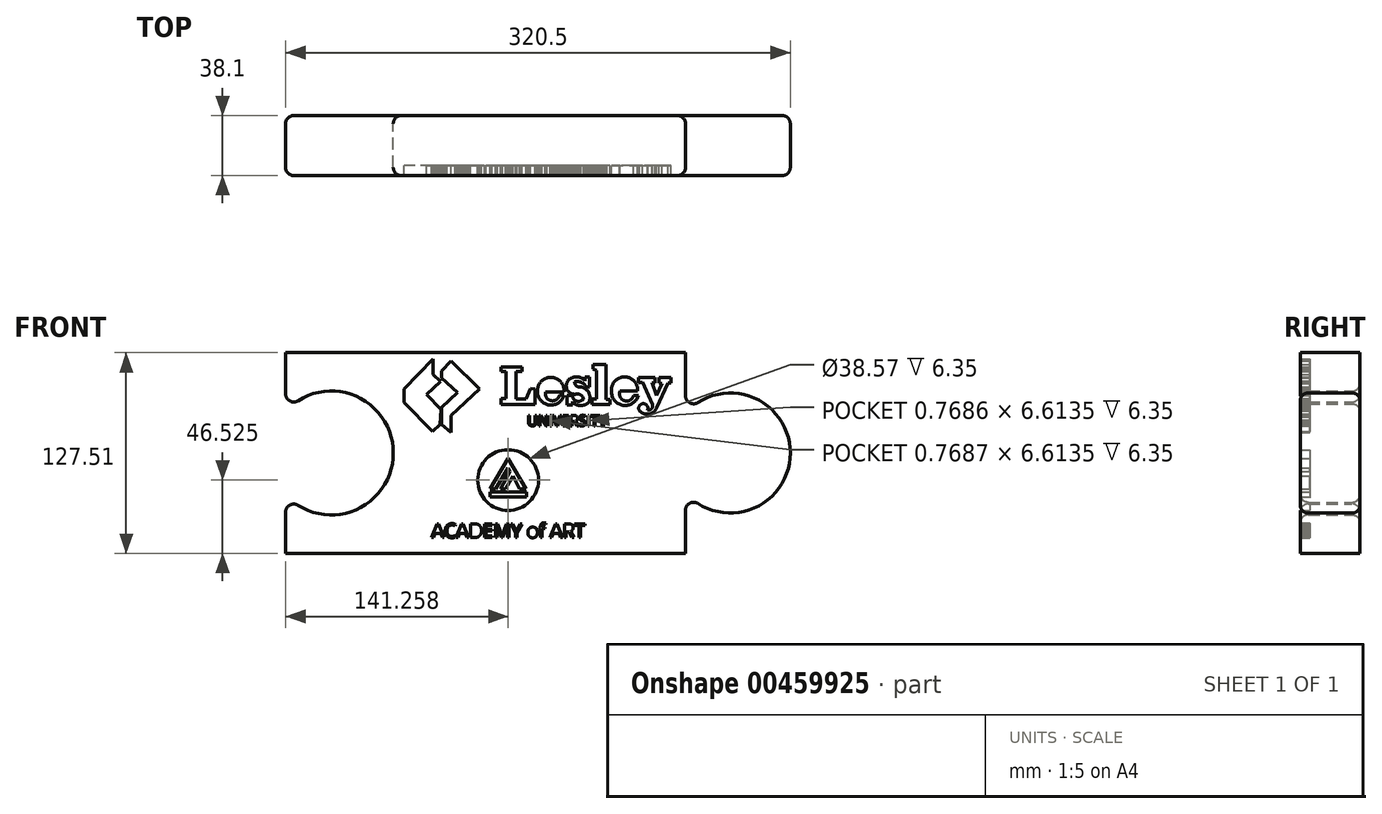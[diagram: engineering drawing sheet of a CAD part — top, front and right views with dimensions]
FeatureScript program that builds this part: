
annotation { "Feature Type Name" : "Feature", "Feature Type Description" : "" }
export const myFeature = defineFeature(function(context is Context, id is Id, definition is map)
    precondition{}
    {
        {
            var Q0;
            Q0=qCreatedBy(makeId("Front.planeOp"),FACE);
            var sketch = newSketch(context, id + "F0", { "sketchPlane" : qUnion([Q0])});
            skLineSegment(sketch, "E0", {"start": v(-231.22, 105.6) * mm, "end": v(22.78, 105.6) * mm});
            skLineSegment(sketch, "E1", {"start": v(-231.22, -21.9) * mm, "end": v(22.78, -21.9) * mm});
            skArc(sketch, "E2", {"start": v(22.78, 16.45) * mm, "mid": v(89.28, 41.85) * mm, "end": v(22.78, 67.25) * mm});
            skLineSegment(sketch, "E3", {"start": v(22.78, 67.25) * mm, "end": v(22.78, 105.6) * mm});
            skLineSegment(sketch, "E4", {"start": v(22.78, 16.45) * mm, "end": v(22.78, -21.9) * mm});
            skArc(sketch, "E5", {"start": v(-231.22, 15.18) * mm, "mid": v(-162.9, 41.85) * mm, "end": v(-231.22, 68.52) * mm});
            skLineSegment(sketch, "E6", {"start": v(-231.22, 15.18) * mm, "end": v(-231.22, -21.9) * mm});
            skLineSegment(sketch, "E7", {"start": v(-231.22, 68.52) * mm, "end": v(-231.22, 105.6) * mm});
            skCircle(sketch, "E8", {"center": v(-89.96, 24.62) * mm, "radius": 19.29 * mm});
            skText(sketch, "E9", { "text": "ACADEMY of ART", "fontName": "OpenSans-Regular.ttf"});
            skLineSegment(sketch, "E10", {"start": v(-132.08, 89.6) * mm, "end": v(-122.02, 80.37) * mm});
            skLineSegment(sketch, "E11", {"start": v(-132.08, 89.6) * mm, "end": v(-132.08, 94.1) * mm});
            skLineSegment(sketch, "E12", {"start": v(-132.08, 94.1) * mm, "end": v(-119.6, 82.65) * mm});
            skLineSegment(sketch, "E13", {"start": v(-119.6, 82.65) * mm, "end": v(-132.08, 70.9) * mm});
            skLineSegment(sketch, "E14", {"start": v(-132.08, 70.9) * mm, "end": v(-126.27, 65.56) * mm});
            skLineSegment(sketch, "E15", {"start": v(-126.27, 65.56) * mm, "end": v(-126.27, 54.88) * mm});
            skLineSegment(sketch, "E16", {"start": v(-126.27, 54.88) * mm, "end": v(-107.94, 73.88) * mm});
            skLineSegment(sketch, "E17", {"start": v(-108.11, 73.7) * mm, "end": v(-108.11, 82.65) * mm});
            skLineSegment(sketch, "E18", {"start": v(-108.11, 82.65) * mm, "end": v(-126.27, 65.56) * mm});
            skLineSegment(sketch, "E19", {"start": v(-132.08, 94.1) * mm, "end": v(-126.27, 100.43) * mm});
            skLineSegment(sketch, "E20", {"start": v(-126.27, 100.43) * mm, "end": v(-108.11, 82.65) * mm});
            skLineSegment(sketch, "E21", {"start": v(-137.7, 101.62) * mm, "end": v(-137.7, 91.84) * mm});
            skPoint(sketch, "E21.endSnap0", {"position": v(-132.08, 91.84) * mm});
            skLineSegment(sketch, "E22", {"start": v(-137.7, 91.84) * mm, "end": v(-156.08, 73.88) * mm});
            skPoint(sketch, "E22.endSnap0", {"position": v(-156.08, 78.25) * mm});
            skLineSegment(sketch, "E23", {"start": v(-156.08, 82.65) * mm, "end": v(-156.08, 73.88) * mm});
            skLineSegment(sketch, "E24", {"start": v(-156.08, 82.65) * mm, "end": v(-137.7, 101.62) * mm});
            skLineSegment(sketch, "E25", {"start": v(-156.08, 73.88) * mm, "end": v(-138, 55.4) * mm});
            skLineSegment(sketch, "E26", {"start": v(-138, 55.4) * mm, "end": v(-133.18, 60.1) * mm});
            skLineSegment(sketch, "E27", {"start": v(-132.08, 70.9) * mm, "end": v(-132.08, 60.1) * mm});
            skLineSegment(sketch, "E28", {"start": v(-132.08, 60.1) * mm, "end": v(-126.27, 54.88) * mm});
            skLineSegment(sketch, "E29", {"start": v(-146.49, 73.88) * mm, "end": v(-133.18, 60.1) * mm});
            skLineSegment(sketch, "E30", {"start": v(-94.5, 93.55) * mm, "end": v(-94.5, 96.58) * mm});
            skLineSegment(sketch, "E31", {"start": v(-94.5, 96.58) * mm, "end": v(-81.08, 96.58) * mm});
            skLineSegment(sketch, "E32", {"start": v(-81.08, 96.58) * mm, "end": v(-81.08, 93.77) * mm});
            skLineSegment(sketch, "E33", {"start": v(-81.08, 93.77) * mm, "end": v(-85.05, 93.77) * mm});
            skLineSegment(sketch, "E34", {"start": v(-85.05, 93.77) * mm, "end": v(-85.05, 76.1) * mm});
            skLineSegment(sketch, "E35", {"start": v(-85.05, 76.1) * mm, "end": v(-78.52, 76.1) * mm});
            skLineSegment(sketch, "E36", {"start": v(-78.52, 76.1) * mm, "end": v(-75.83, 82.81) * mm});
            skLineSegment(sketch, "E37", {"start": v(-94.5, 93.55) * mm, "end": v(-91.3, 93.55) * mm});
            skLineSegment(sketch, "E38", {"start": v(-91.3, 93.55) * mm, "end": v(-91.3, 76.56) * mm});
            skLineSegment(sketch, "E39", {"start": v(-91.3, 76.56) * mm, "end": v(-94.5, 76.56) * mm});
            skLineSegment(sketch, "E40", {"start": v(-94.5, 76.56) * mm, "end": v(-94.5, 72.76) * mm});
            skLineSegment(sketch, "E41", {"start": v(-94.5, 72.76) * mm, "end": v(-72.7, 72.76) * mm});
            skLineSegment(sketch, "E42", {"start": v(-72.7, 72.76) * mm, "end": v(-72.7, 82.57) * mm});
            skLineSegment(sketch, "E43", {"start": v(-72.7, 82.57) * mm, "end": v(-75.83, 82.81) * mm});
            skLineSegment(sketch, "E44", {"start": v(-57.35, 78.56) * mm, "end": v(-54.4, 78.56) * mm});
            skLineSegment(sketch, "E45", {"start": v(-65.7, 82.57) * mm, "end": v(-59.8, 82.57) * mm});
            skLineSegment(sketch, "E46", {"start": v(-66.16, 80.54) * mm, "end": v(-54.4, 80.54) * mm});
            skArc(sketch, "E47", {"start": v(-59.8, 82.57) * mm, "mid": v(-62.76, 87.36) * mm, "end": v(-65.7, 82.57) * mm});
            skArc(sketch, "E48", {"start": v(-54.4, 80.54) * mm, "mid": v(-62.85, 89.89) * mm, "end": v(-71.3, 80.54) * mm});
            skArc(sketch, "E49", {"start": v(-71.3, 80.54) * mm, "mid": v(-63.7, 72.33) * mm, "end": v(-54.4, 78.56) * mm});
            skArc(sketch, "E50", {"start": v(-66.16, 80.54) * mm, "mid": v(-62.75, 75.11) * mm, "end": v(-57.35, 78.56) * mm});
            skLineSegment(sketch, "E51", {"start": v(-18.82, 81.15) * mm, "end": v(-7.64, 81.15) * mm});
            skLineSegment(sketch, "E52", {"start": v(-19.2, 83.23) * mm, "end": v(-12.95, 83.23) * mm});
            skLineSegment(sketch, "E53", {"start": v(-10.3, 78.5) * mm, "end": v(-7.26, 78.5) * mm});
            skLineSegment(sketch, "E54", {"start": v(-40.4, 83.88) * mm, "end": v(-38.13, 83.88) * mm});
            skLineSegment(sketch, "E55", {"start": v(-38.13, 83.88) * mm, "end": v(-38.13, 90.14) * mm});
            skLineSegment(sketch, "E56", {"start": v(-38.13, 90.14) * mm, "end": v(-40.97, 90.14) * mm});
            skLineSegment(sketch, "E57", {"start": v(-40.97, 90.14) * mm, "end": v(-40.97, 87.68) * mm});
            skLineSegment(sketch, "E58", {"start": v(-49.16, 74.51) * mm, "end": v(-49.16, 72.24) * mm});
            skLineSegment(sketch, "E59", {"start": v(-49.16, 72.24) * mm, "end": v(-52.58, 72.24) * mm});
            skLineSegment(sketch, "E60", {"start": v(-52.58, 72.24) * mm, "end": v(-52.58, 78.5) * mm});
            skLineSegment(sketch, "E61", {"start": v(-52.58, 78.5) * mm, "end": v(-49.16, 78.5) * mm});
            skLineSegment(sketch, "E62", {"start": v(-36.08, 95.18) * mm, "end": v(-36.08, 98.21) * mm});
            skLineSegment(sketch, "E63", {"start": v(-36.08, 98.21) * mm, "end": v(-27.93, 98.21) * mm});
            skLineSegment(sketch, "E64", {"start": v(-27.93, 98.21) * mm, "end": v(-27.93, 75.84) * mm});
            skLineSegment(sketch, "E65", {"start": v(-27.93, 75.84) * mm, "end": v(-25.08, 75.84) * mm});
            skLineSegment(sketch, "E66", {"start": v(-25.08, 75.84) * mm, "end": v(-25.08, 72.8) * mm});
            skLineSegment(sketch, "E67", {"start": v(-25.08, 72.8) * mm, "end": v(-36.65, 72.8) * mm});
            skLineSegment(sketch, "E68", {"start": v(-36.65, 72.8) * mm, "end": v(-36.65, 76.03) * mm});
            skLineSegment(sketch, "E69", {"start": v(-36.65, 76.03) * mm, "end": v(-33.8, 76.03) * mm});
            skLineSegment(sketch, "E70", {"start": v(-33.8, 76.03) * mm, "end": v(-33.8, 94.23) * mm});
            skLineSegment(sketch, "E71", {"start": v(-33.8, 94.23) * mm, "end": v(-36.08, 95.18) * mm});
            skLineSegment(sketch, "E72", {"start": v(1.53, 86.65) * mm, "end": v(4.3, 78.3) * mm});
            skLineSegment(sketch, "E73", {"start": v(4.3, 78.3) * mm, "end": v(7.91, 86.08) * mm});
            skLineSegment(sketch, "E74", {"start": v(6.02, 86.27) * mm, "end": v(7.91, 86.08) * mm});
            skLineSegment(sketch, "E75", {"start": v(6.02, 86.27) * mm, "end": v(6.02, 89.68) * mm});
            skLineSegment(sketch, "E76", {"start": v(6.02, 89.68) * mm, "end": v(13.43, 89.68) * mm});
            skLineSegment(sketch, "E77", {"start": v(13.43, 89.68) * mm, "end": v(13.43, 86.27) * mm});
            skLineSegment(sketch, "E78", {"start": v(13.43, 86.27) * mm, "end": v(11.7, 86.27) * mm});
            skLineSegment(sketch, "E79", {"start": v(11.7, 86.27) * mm, "end": v(4.3, 70.34) * mm});
            skLineSegment(sketch, "E80", {"start": v(1.62, 72.78) * mm, "end": v(-4.6, 86.84) * mm});
            skLineSegment(sketch, "E81", {"start": v(1.53, 86.65) * mm, "end": v(3.36, 86.27) * mm});
            skLineSegment(sketch, "E82", {"start": v(3.36, 86.27) * mm, "end": v(3.36, 89.68) * mm});
            skLineSegment(sketch, "E83", {"start": v(3.36, 89.68) * mm, "end": v(-7.26, 89.68) * mm});
            skLineSegment(sketch, "E84", {"start": v(-7.26, 89.68) * mm, "end": v(-7.26, 86.27) * mm});
            skLineSegment(sketch, "E85", {"start": v(-7.26, 86.27) * mm, "end": v(-4.6, 86.84) * mm});
            skArc(sketch, "E86", {"start": v(-1.38, 69.2) * mm, "mid": v(1.24, 70.06) * mm, "end": v(1.62, 72.78) * mm});
            skArc(sketch, "E87", {"start": v(-6.5, 68.63) * mm, "mid": v(-0.64, 66.6) * mm, "end": v(4.3, 70.34) * mm});
            skArc(sketch, "E88", {"start": v(-7.64, 81.15) * mm, "mid": v(-15.98, 90.2) * mm, "end": v(-24.32, 81.15) * mm});
            skArc(sketch, "E89", {"start": v(-24.32, 81.15) * mm, "mid": v(-16.98, 72.19) * mm, "end": v(-7.26, 78.5) * mm});
            skArc(sketch, "E90", {"start": v(-18.82, 81.15) * mm, "mid": v(-16.04, 75.07) * mm, "end": v(-10.3, 78.5) * mm});
            skArc(sketch, "E91", {"start": v(-12.95, 83.23) * mm, "mid": v(-16.07, 87.66) * mm, "end": v(-19.2, 83.23) * mm});
            skArc(sketch, "E92", {"start": v(-49.16, 78.5) * mm, "mid": v(-46.47, 74.84) * mm, "end": v(-42.15, 76.22) * mm});
            skArc(sketch, "E93", {"start": v(-42.15, 76.22) * mm, "mid": v(-43.8, 78.75) * mm, "end": v(-46.77, 79.23) * mm});
            skArc(sketch, "E94", {"start": v(-49.27, 89.73) * mm, "mid": v(-52.9, 83.32) * mm, "end": v(-46.77, 79.23) * mm});
            skArc(sketch, "E95", {"start": v(-40.97, 87.68) * mm, "mid": v(-44.79, 90.07) * mm, "end": v(-49.27, 89.73) * mm});
            skArc(sketch, "E96", {"start": v(-40.4, 83.88) * mm, "mid": v(-43.46, 86.77) * mm, "end": v(-47.65, 87) * mm});
            skArc(sketch, "E97", {"start": v(-47.65, 87) * mm, "mid": v(-46.56, 84.41) * mm, "end": v(-43.8, 83.88) * mm});
            skArc(sketch, "E98", {"start": v(-49.16, 74.51) * mm, "mid": v(-43.8, 71.98) * mm, "end": v(-38.45, 74.51) * mm});
            skArc(sketch, "E99", {"start": v(-38.45, 74.51) * mm, "mid": v(-38.9, 80.47) * mm, "end": v(-43.8, 83.88) * mm});
            skText(sketch, "E100", { "text": "UNIVERSITY\n", "fontName": "OpenSans-Regular.ttf"});
            skLineSegment(sketch, "E101", {"start": v(-137.7, 101.62) * mm, "end": v(-132.98, 97.04) * mm});
            skLineSegment(sketch, "E102", {"start": v(-132.96, 97.08) * mm, "end": v(-132.96, 87.22) * mm});
            skLineSegment(sketch, "E103", {"start": v(-132.87, 87.4) * mm, "end": v(-141.86, 78.93) * mm});
            skLineSegment(sketch, "E104", {"start": v(-146.49, 73.88) * mm, "end": v(-141.86, 78.93) * mm});
            skLineSegment(sketch, "E105", {"start": v(-137.7, 91.84) * mm, "end": v(-132.87, 87.4) * mm});
            skLineSegment(sketch, "E106", {"start": v(-133.18, 60.1) * mm, "end": v(-132.63, 69.43) * mm});
            skLineSegment(sketch, "E107", {"start": v(-141.86, 78.93) * mm, "end": v(-132.63, 69.43) * mm});
            skArc(sketch, "E108", {"start": v(-1.38, 69.2) * mm, "mid": v(-4.41, 73.2) * mm, "end": v(-6.5, 68.63) * mm});
            const initialGuessF0  = {"E9": [-0.13842, -0.01189, 1, 0, 0.00886], "E100": [-0.07792, 0.05915, 1, 0, 0.00667]};
            skSetInitialGuess(sketch, initialGuessF0);
            skSolve(sketch);
        }
        {
            var Q0;
            Q0 = qSketchRegion(id + "F0", true);
            extrude(context, id + "F1", {"entities" : qUnion([Q0]), "depth" : 38.1 * mm});
        }
        {
            var Q0;
            Q0=makeQuery(id+"F1.opExtrude","CAP_FACE",FACE,{"disambiguationData":[OSD([sQuery(id+"F0.wireOp",EDGE,"E0"),sQuery(id+"F0.wireOp",EDGE,"E1"),sQuery(id+"F0.wireOp",EDGE,"E2"),sQuery(id+"F0.wireOp",EDGE,"E3"),sQuery(id+"F0.wireOp",EDGE,"E4"),sQuery(id+"F0.wireOp",EDGE,"E5"),sQuery(id+"F0.wireOp",EDGE,"E6"),sQuery(id+"F0.wireOp",EDGE,"E7"),sQuery(id+"F0.wireOp",EDGE,"E8"),sQuery(id+"F0.wireOp",EDGE,"E9.sketch_text.stroke-0"),sQuery(id+"F0.wireOp",EDGE,"E9.sketch_text.stroke-1"),sQuery(id+"F0.wireOp",EDGE,"E9.sketch_text.stroke-2"),sQuery(id+"F0.wireOp",EDGE,"E9.sketch_text.stroke-3"),sQuery(id+"F0.wireOp",EDGE,"E9.sketch_text.stroke-4"),sQuery(id+"F0.wireOp",EDGE,"E9.sketch_text.stroke-5"),sQuery(id+"F0.wireOp",EDGE,"E9.sketch_text.stroke-6"),sQuery(id+"F0.wireOp",EDGE,"E9.sketch_text.stroke-7"),sQuery(id+"F0.wireOp",EDGE,"E9.sketch_text.stroke-13"),sQuery(id+"F0.wireOp",EDGE,"E9.sketch_text.stroke-14"),sQuery(id+"F0.wireOp",EDGE,"E9.sketch_text.stroke-15"),sQuery(id+"F0.wireOp",EDGE,"E9.sketch_text.stroke-16"),sQuery(id+"F0.wireOp",EDGE,"E9.sketch_text.stroke-17"),sQuery(id+"F0.wireOp",EDGE,"E9.sketch_text.stroke-18"),sQuery(id+"F0.wireOp",EDGE,"E9.sketch_text.stroke-19"),sQuery(id+"F0.wireOp",EDGE,"E9.sketch_text.stroke-20"),sQuery(id+"F0.wireOp",EDGE,"E9.sketch_text.stroke-21"),sQuery(id+"F0.wireOp",EDGE,"E9.sketch_text.stroke-22"),sQuery(id+"F0.wireOp",EDGE,"E9.sketch_text.stroke-23"),sQuery(id+"F0.wireOp",EDGE,"E9.sketch_text.stroke-24"),sQuery(id+"F0.wireOp",EDGE,"E9.sketch_text.stroke-25"),sQuery(id+"F0.wireOp",EDGE,"E9.sketch_text.stroke-26"),sQuery(id+"F0.wireOp",EDGE,"E9.sketch_text.stroke-27"),sQuery(id+"F0.wireOp",EDGE,"E9.sketch_text.stroke-28"),sQuery(id+"F0.wireOp",EDGE,"E9.sketch_text.stroke-29"),sQuery(id+"F0.wireOp",EDGE,"E9.sketch_text.stroke-30"),sQuery(id+"F0.wireOp",EDGE,"E9.sketch_text.stroke-31"),sQuery(id+"F0.wireOp",EDGE,"E9.sketch_text.stroke-32"),sQuery(id+"F0.wireOp",EDGE,"E9.sketch_text.stroke-33"),sQuery(id+"F0.wireOp",EDGE,"E9.sketch_text.stroke-34"),sQuery(id+"F0.wireOp",EDGE,"E9.sketch_text.stroke-35"),sQuery(id+"F0.wireOp",EDGE,"E9.sketch_text.stroke-41"),sQuery(id+"F0.wireOp",EDGE,"E9.sketch_text.stroke-42"),sQuery(id+"F0.wireOp",EDGE,"E9.sketch_text.stroke-43"),sQuery(id+"F0.wireOp",EDGE,"E9.sketch_text.stroke-44"),sQuery(id+"F0.wireOp",EDGE,"E9.sketch_text.stroke-45"),sQuery(id+"F0.wireOp",EDGE,"E9.sketch_text.stroke-46"),sQuery(id+"F0.wireOp",EDGE,"E9.sketch_text.stroke-47"),sQuery(id+"F0.wireOp",EDGE,"E9.sketch_text.stroke-55"),sQuery(id+"F0.wireOp",EDGE,"E9.sketch_text.stroke-56"),sQuery(id+"F0.wireOp",EDGE,"E9.sketch_text.stroke-57"),sQuery(id+"F0.wireOp",EDGE,"E9.sketch_text.stroke-58"),sQuery(id+"F0.wireOp",EDGE,"E9.sketch_text.stroke-59"),sQuery(id+"F0.wireOp",EDGE,"E9.sketch_text.stroke-60"),sQuery(id+"F0.wireOp",EDGE,"E9.sketch_text.stroke-61"),sQuery(id+"F0.wireOp",EDGE,"E9.sketch_text.stroke-62"),sQuery(id+"F0.wireOp",EDGE,"E9.sketch_text.stroke-63"),sQuery(id+"F0.wireOp",EDGE,"E9.sketch_text.stroke-64"),sQuery(id+"F0.wireOp",EDGE,"E9.sketch_text.stroke-65"),sQuery(id+"F0.wireOp",EDGE,"E9.sketch_text.stroke-66"),sQuery(id+"F0.wireOp",EDGE,"E9.sketch_text.stroke-67"),sQuery(id+"F0.wireOp",EDGE,"E9.sketch_text.stroke-68"),sQuery(id+"F0.wireOp",EDGE,"E9.sketch_text.stroke-69"),sQuery(id+"F0.wireOp",EDGE,"E9.sketch_text.stroke-70"),sQuery(id+"F0.wireOp",EDGE,"E9.sketch_text.stroke-71"),sQuery(id+"F0.wireOp",EDGE,"E9.sketch_text.stroke-72"),sQuery(id+"F0.wireOp",EDGE,"E9.sketch_text.stroke-73"),sQuery(id+"F0.wireOp",EDGE,"E9.sketch_text.stroke-74"),sQuery(id+"F0.wireOp",EDGE,"E9.sketch_text.stroke-75"),sQuery(id+"F0.wireOp",EDGE,"E9.sketch_text.stroke-76"),sQuery(id+"F0.wireOp",EDGE,"E9.sketch_text.stroke-77"),sQuery(id+"F0.wireOp",EDGE,"E9.sketch_text.stroke-78"),sQuery(id+"F0.wireOp",EDGE,"E9.sketch_text.stroke-79"),sQuery(id+"F0.wireOp",EDGE,"E9.sketch_text.stroke-80"),sQuery(id+"F0.wireOp",EDGE,"E9.sketch_text.stroke-81"),sQuery(id+"F0.wireOp",EDGE,"E9.sketch_text.stroke-82"),sQuery(id+"F0.wireOp",EDGE,"E9.sketch_text.stroke-83"),sQuery(id+"F0.wireOp",EDGE,"E9.sketch_text.stroke-84"),sQuery(id+"F0.wireOp",EDGE,"E9.sketch_text.stroke-85"),sQuery(id+"F0.wireOp",EDGE,"E9.sketch_text.stroke-86"),sQuery(id+"F0.wireOp",EDGE,"E9.sketch_text.stroke-87"),sQuery(id+"F0.wireOp",EDGE,"E9.sketch_text.stroke-88"),sQuery(id+"F0.wireOp",EDGE,"E9.sketch_text.stroke-89"),sQuery(id+"F0.wireOp",EDGE,"E9.sketch_text.stroke-90"),sQuery(id+"F0.wireOp",EDGE,"E9.sketch_text.stroke-91"),sQuery(id+"F0.wireOp",EDGE,"E9.sketch_text.stroke-92"),sQuery(id+"F0.wireOp",EDGE,"E9.sketch_text.stroke-93"),sQuery(id+"F0.wireOp",EDGE,"E9.sketch_text.stroke-94"),sQuery(id+"F0.wireOp",EDGE,"E9.sketch_text.stroke-95"),sQuery(id+"F0.wireOp",EDGE,"E9.sketch_text.stroke-96"),sQuery(id+"F0.wireOp",EDGE,"E9.sketch_text.stroke-97"),sQuery(id+"F0.wireOp",EDGE,"E9.sketch_text.stroke-98"),sQuery(id+"F0.wireOp",EDGE,"E9.sketch_text.stroke-99"),sQuery(id+"F0.wireOp",EDGE,"E9.sketch_text.stroke-100"),sQuery(id+"F0.wireOp",EDGE,"E9.sketch_text.stroke-101"),sQuery(id+"F0.wireOp",EDGE,"E9.sketch_text.stroke-102"),sQuery(id+"F0.wireOp",EDGE,"E9.sketch_text.stroke-111"),sQuery(id+"F0.wireOp",EDGE,"E9.sketch_text.stroke-112"),sQuery(id+"F0.wireOp",EDGE,"E9.sketch_text.stroke-113"),sQuery(id+"F0.wireOp",EDGE,"E9.sketch_text.stroke-114"),sQuery(id+"F0.wireOp",EDGE,"E9.sketch_text.stroke-115"),sQuery(id+"F0.wireOp",EDGE,"E9.sketch_text.stroke-116"),sQuery(id+"F0.wireOp",EDGE,"E9.sketch_text.stroke-117"),sQuery(id+"F0.wireOp",EDGE,"E9.sketch_text.stroke-118"),sQuery(id+"F0.wireOp",EDGE,"E9.sketch_text.stroke-119"),sQuery(id+"F0.wireOp",EDGE,"E9.sketch_text.stroke-120"),sQuery(id+"F0.wireOp",EDGE,"E9.sketch_text.stroke-121"),sQuery(id+"F0.wireOp",EDGE,"E9.sketch_text.stroke-122"),sQuery(id+"F0.wireOp",EDGE,"E9.sketch_text.stroke-123"),sQuery(id+"F0.wireOp",EDGE,"E9.sketch_text.stroke-124"),sQuery(id+"F0.wireOp",EDGE,"E9.sketch_text.stroke-125"),sQuery(id+"F0.wireOp",EDGE,"E9.sketch_text.stroke-126"),sQuery(id+"F0.wireOp",EDGE,"E9.sketch_text.stroke-127"),sQuery(id+"F0.wireOp",EDGE,"E9.sketch_text.stroke-128"),sQuery(id+"F0.wireOp",EDGE,"E9.sketch_text.stroke-129"),sQuery(id+"F0.wireOp",EDGE,"E9.sketch_text.stroke-130"),sQuery(id+"F0.wireOp",EDGE,"E9.sketch_text.stroke-131"),sQuery(id+"F0.wireOp",EDGE,"E9.sketch_text.stroke-132"),sQuery(id+"F0.wireOp",EDGE,"E9.sketch_text.stroke-133"),sQuery(id+"F0.wireOp",EDGE,"E9.sketch_text.stroke-134"),sQuery(id+"F0.wireOp",EDGE,"E9.sketch_text.stroke-135"),sQuery(id+"F0.wireOp",EDGE,"E9.sketch_text.stroke-141"),sQuery(id+"F0.wireOp",EDGE,"E9.sketch_text.stroke-142"),sQuery(id+"F0.wireOp",EDGE,"E9.sketch_text.stroke-143"),sQuery(id+"F0.wireOp",EDGE,"E9.sketch_text.stroke-144"),sQuery(id+"F0.wireOp",EDGE,"E9.sketch_text.stroke-145"),sQuery(id+"F0.wireOp",EDGE,"E9.sketch_text.stroke-146"),sQuery(id+"F0.wireOp",EDGE,"E9.sketch_text.stroke-147"),sQuery(id+"F0.wireOp",EDGE,"E9.sketch_text.stroke-148"),sQuery(id+"F0.wireOp",EDGE,"E9.sketch_text.stroke-149"),sQuery(id+"F0.wireOp",EDGE,"E9.sketch_text.stroke-150"),sQuery(id+"F0.wireOp",EDGE,"E9.sketch_text.stroke-151"),sQuery(id+"F0.wireOp",EDGE,"E9.sketch_text.stroke-159"),sQuery(id+"F0.wireOp",EDGE,"E9.sketch_text.stroke-160"),sQuery(id+"F0.wireOp",EDGE,"E9.sketch_text.stroke-161"),sQuery(id+"F0.wireOp",EDGE,"E9.sketch_text.stroke-162"),sQuery(id+"F0.wireOp",EDGE,"E9.sketch_text.stroke-163"),sQuery(id+"F0.wireOp",EDGE,"E9.sketch_text.stroke-164"),sQuery(id+"F0.wireOp",EDGE,"E9.sketch_text.stroke-165"),sQuery(id+"F0.wireOp",EDGE,"E9.sketch_text.stroke-166"),sQuery(id+"F0.wireOp",EDGE,"E10"),sQuery(id+"F0.wireOp",EDGE,"E11"),sQuery(id+"F0.wireOp",EDGE,"E13"),sQuery(id+"F0.wireOp",EDGE,"E15"),sQuery(id+"F0.wireOp",EDGE,"E18"),sQuery(id+"F0.wireOp",EDGE,"E19"),sQuery(id+"F0.wireOp",EDGE,"E20"),sQuery(id+"F0.wireOp",EDGE,"E21"),sQuery(id+"F0.wireOp",EDGE,"E23"),sQuery(id+"F0.wireOp",EDGE,"E24"),sQuery(id+"F0.wireOp",EDGE,"E25"),sQuery(id+"F0.wireOp",EDGE,"E26"),sQuery(id+"F0.wireOp",EDGE,"E27"),sQuery(id+"F0.wireOp",EDGE,"E28"),sQuery(id+"F0.wireOp",EDGE,"E30"),sQuery(id+"F0.wireOp",EDGE,"E31"),sQuery(id+"F0.wireOp",EDGE,"E32"),sQuery(id+"F0.wireOp",EDGE,"E33"),sQuery(id+"F0.wireOp",EDGE,"E34"),sQuery(id+"F0.wireOp",EDGE,"E35"),sQuery(id+"F0.wireOp",EDGE,"E36"),sQuery(id+"F0.wireOp",EDGE,"E37"),sQuery(id+"F0.wireOp",EDGE,"E38"),sQuery(id+"F0.wireOp",EDGE,"E39"),sQuery(id+"F0.wireOp",EDGE,"E40"),sQuery(id+"F0.wireOp",EDGE,"E41"),sQuery(id+"F0.wireOp",EDGE,"E42"),sQuery(id+"F0.wireOp",EDGE,"E43"),sQuery(id+"F0.wireOp",EDGE,"E44"),sQuery(id+"F0.wireOp",EDGE,"E46"),sQuery(id+"F0.wireOp",EDGE,"E48"),sQuery(id+"F0.wireOp",EDGE,"E49"),sQuery(id+"F0.wireOp",EDGE,"E50"),sQuery(id+"F0.wireOp",EDGE,"E51"),sQuery(id+"F0.wireOp",EDGE,"E53"),sQuery(id+"F0.wireOp",EDGE,"E54"),sQuery(id+"F0.wireOp",EDGE,"E55"),sQuery(id+"F0.wireOp",EDGE,"E56"),sQuery(id+"F0.wireOp",EDGE,"E57"),sQuery(id+"F0.wireOp",EDGE,"E58"),sQuery(id+"F0.wireOp",EDGE,"E59"),sQuery(id+"F0.wireOp",EDGE,"E60"),sQuery(id+"F0.wireOp",EDGE,"E61"),sQuery(id+"F0.wireOp",EDGE,"E62"),sQuery(id+"F0.wireOp",EDGE,"E63"),sQuery(id+"F0.wireOp",EDGE,"E64"),sQuery(id+"F0.wireOp",EDGE,"E65"),sQuery(id+"F0.wireOp",EDGE,"E66"),sQuery(id+"F0.wireOp",EDGE,"E67"),sQuery(id+"F0.wireOp",EDGE,"E68"),sQuery(id+"F0.wireOp",EDGE,"E69"),sQuery(id+"F0.wireOp",EDGE,"E70"),sQuery(id+"F0.wireOp",EDGE,"E71"),sQuery(id+"F0.wireOp",EDGE,"E88"),sQuery(id+"F0.wireOp",EDGE,"E89"),sQuery(id+"F0.wireOp",EDGE,"E90"),sQuery(id+"F0.wireOp",EDGE,"E92"),sQuery(id+"F0.wireOp",EDGE,"E93"),sQuery(id+"F0.wireOp",EDGE,"E94"),sQuery(id+"F0.wireOp",EDGE,"E95"),sQuery(id+"F0.wireOp",EDGE,"E96"),sQuery(id+"F0.wireOp",EDGE,"E97"),sQuery(id+"F0.wireOp",EDGE,"E98"),sQuery(id+"F0.wireOp",EDGE,"E99"),sQuery(id+"F0.wireOp",EDGE,"E100.sketch_text.stroke-0"),sQuery(id+"F0.wireOp",EDGE,"E100.sketch_text.stroke-1"),sQuery(id+"F0.wireOp",EDGE,"E100.sketch_text.stroke-2"),sQuery(id+"F0.wireOp",EDGE,"E100.sketch_text.stroke-3"),sQuery(id+"F0.wireOp",EDGE,"E100.sketch_text.stroke-4"),sQuery(id+"F0.wireOp",EDGE,"E100.sketch_text.stroke-5"),sQuery(id+"F0.wireOp",EDGE,"E100.sketch_text.stroke-6"),sQuery(id+"F0.wireOp",EDGE,"E100.sketch_text.stroke-7"),sQuery(id+"F0.wireOp",EDGE,"E100.sketch_text.stroke-8"),sQuery(id+"F0.wireOp",EDGE,"E100.sketch_text.stroke-9"),sQuery(id+"F0.wireOp",EDGE,"E100.sketch_text.stroke-10"),sQuery(id+"F0.wireOp",EDGE,"E100.sketch_text.stroke-11"),sQuery(id+"F0.wireOp",EDGE,"E100.sketch_text.stroke-12"),sQuery(id+"F0.wireOp",EDGE,"E100.sketch_text.stroke-13"),sQuery(id+"F0.wireOp",EDGE,"E100.sketch_text.stroke-14"),sQuery(id+"F0.wireOp",EDGE,"E100.sketch_text.stroke-15"),sQuery(id+"F0.wireOp",EDGE,"E100.sketch_text.stroke-16"),sQuery(id+"F0.wireOp",EDGE,"E100.sketch_text.stroke-17"),sQuery(id+"F0.wireOp",EDGE,"E100.sketch_text.stroke-18"),sQuery(id+"F0.wireOp",EDGE,"E100.sketch_text.stroke-19"),sQuery(id+"F0.wireOp",EDGE,"E100.sketch_text.stroke-20"),sQuery(id+"F0.wireOp",EDGE,"E100.sketch_text.stroke-21"),sQuery(id+"F0.wireOp",EDGE,"E100.sketch_text.stroke-22"),sQuery(id+"F0.wireOp",EDGE,"E100.sketch_text.stroke-23"),sQuery(id+"F0.wireOp",EDGE,"E100.sketch_text.stroke-24"),sQuery(id+"F0.wireOp",EDGE,"E100.sketch_text.stroke-25"),sQuery(id+"F0.wireOp",EDGE,"E100.sketch_text.stroke-26"),sQuery(id+"F0.wireOp",EDGE,"E100.sketch_text.stroke-27"),sQuery(id+"F0.wireOp",EDGE,"E100.sketch_text.stroke-28"),sQuery(id+"F0.wireOp",EDGE,"E100.sketch_text.stroke-29"),sQuery(id+"F0.wireOp",EDGE,"E100.sketch_text.stroke-30"),sQuery(id+"F0.wireOp",EDGE,"E100.sketch_text.stroke-31"),sQuery(id+"F0.wireOp",EDGE,"E100.sketch_text.stroke-32"),sQuery(id+"F0.wireOp",EDGE,"E100.sketch_text.stroke-33"),sQuery(id+"F0.wireOp",EDGE,"E100.sketch_text.stroke-34"),sQuery(id+"F0.wireOp",EDGE,"E100.sketch_text.stroke-35"),sQuery(id+"F0.wireOp",EDGE,"E100.sketch_text.stroke-36"),sQuery(id+"F0.wireOp",EDGE,"E100.sketch_text.stroke-37"),sQuery(id+"F0.wireOp",EDGE,"E100.sketch_text.stroke-38"),sQuery(id+"F0.wireOp",EDGE,"E100.sketch_text.stroke-39"),sQuery(id+"F0.wireOp",EDGE,"E100.sketch_text.stroke-40"),sQuery(id+"F0.wireOp",EDGE,"E100.sketch_text.stroke-41"),sQuery(id+"F0.wireOp",EDGE,"E100.sketch_text.stroke-42"),sQuery(id+"F0.wireOp",EDGE,"E100.sketch_text.stroke-43"),sQuery(id+"F0.wireOp",EDGE,"E100.sketch_text.stroke-44"),sQuery(id+"F0.wireOp",EDGE,"E100.sketch_text.stroke-45"),sQuery(id+"F0.wireOp",EDGE,"E100.sketch_text.stroke-46"),sQuery(id+"F0.wireOp",EDGE,"E100.sketch_text.stroke-47"),sQuery(id+"F0.wireOp",EDGE,"E100.sketch_text.stroke-48"),sQuery(id+"F0.wireOp",EDGE,"E100.sketch_text.stroke-49"),sQuery(id+"F0.wireOp",EDGE,"E100.sketch_text.stroke-50"),sQuery(id+"F0.wireOp",EDGE,"E100.sketch_text.stroke-51"),sQuery(id+"F0.wireOp",EDGE,"E100.sketch_text.stroke-52"),sQuery(id+"F0.wireOp",EDGE,"E100.sketch_text.stroke-53"),sQuery(id+"F0.wireOp",EDGE,"E100.sketch_text.stroke-54"),sQuery(id+"F0.wireOp",EDGE,"E100.sketch_text.stroke-55"),sQuery(id+"F0.wireOp",EDGE,"E100.sketch_text.stroke-56"),sQuery(id+"F0.wireOp",EDGE,"E100.sketch_text.stroke-57"),sQuery(id+"F0.wireOp",EDGE,"E100.sketch_text.stroke-58"),sQuery(id+"F0.wireOp",EDGE,"E100.sketch_text.stroke-59"),sQuery(id+"F0.wireOp",EDGE,"E100.sketch_text.stroke-60"),sQuery(id+"F0.wireOp",EDGE,"E100.sketch_text.stroke-61"),sQuery(id+"F0.wireOp",EDGE,"E100.sketch_text.stroke-62"),sQuery(id+"F0.wireOp",EDGE,"E100.sketch_text.stroke-63"),sQuery(id+"F0.wireOp",EDGE,"E100.sketch_text.stroke-64"),sQuery(id+"F0.wireOp",EDGE,"E100.sketch_text.stroke-72"),sQuery(id+"F0.wireOp",EDGE,"E100.sketch_text.stroke-73"),sQuery(id+"F0.wireOp",EDGE,"E100.sketch_text.stroke-74"),sQuery(id+"F0.wireOp",EDGE,"E100.sketch_text.stroke-75"),sQuery(id+"F0.wireOp",EDGE,"E100.sketch_text.stroke-76"),sQuery(id+"F0.wireOp",EDGE,"E100.sketch_text.stroke-77"),sQuery(id+"F0.wireOp",EDGE,"E100.sketch_text.stroke-78"),sQuery(id+"F0.wireOp",EDGE,"E100.sketch_text.stroke-79"),sQuery(id+"F0.wireOp",EDGE,"E100.sketch_text.stroke-80"),sQuery(id+"F0.wireOp",EDGE,"E100.sketch_text.stroke-81"),sQuery(id+"F0.wireOp",EDGE,"E100.sketch_text.stroke-82"),sQuery(id+"F0.wireOp",EDGE,"E100.sketch_text.stroke-83"),sQuery(id+"F0.wireOp",EDGE,"E100.sketch_text.stroke-84"),sQuery(id+"F0.wireOp",EDGE,"E100.sketch_text.stroke-85"),sQuery(id+"F0.wireOp",EDGE,"E100.sketch_text.stroke-86"),sQuery(id+"F0.wireOp",EDGE,"E100.sketch_text.stroke-87"),sQuery(id+"F0.wireOp",EDGE,"E100.sketch_text.stroke-88"),sQuery(id+"F0.wireOp",EDGE,"E100.sketch_text.stroke-89"),sQuery(id+"F0.wireOp",EDGE,"E100.sketch_text.stroke-90"),sQuery(id+"F0.wireOp",EDGE,"E100.sketch_text.stroke-91"),sQuery(id+"F0.wireOp",EDGE,"E100.sketch_text.stroke-92"),sQuery(id+"F0.wireOp",EDGE,"E100.sketch_text.stroke-93"),sQuery(id+"F0.wireOp",EDGE,"E100.sketch_text.stroke-94"),sQuery(id+"F0.wireOp",EDGE,"E100.sketch_text.stroke-95"),sQuery(id+"F0.wireOp",EDGE,"E100.sketch_text.stroke-96"),sQuery(id+"F0.wireOp",EDGE,"E100.sketch_text.stroke-97"),sQuery(id+"F0.wireOp",EDGE,"E100.sketch_text.stroke-98"),sQuery(id+"F0.wireOp",EDGE,"E100.sketch_text.stroke-99"),sQuery(id+"F0.wireOp",EDGE,"E100.sketch_text.stroke-100"),sQuery(id+"F0.wireOp",EDGE,"E100.sketch_text.stroke-101"),sQuery(id+"F0.wireOp",EDGE,"E100.sketch_text.stroke-102"),sQuery(id+"F0.wireOp",EDGE,"E100.sketch_text.stroke-103"),sQuery(id+"F0.wireOp",EDGE,"E100.sketch_text.stroke-104"),sQuery(id+"F0.wireOp",EDGE,"E100.sketch_text.stroke-105"),sQuery(id+"F0.wireOp",EDGE,"E100.sketch_text.stroke-106"),sQuery(id+"F0.wireOp",EDGE,"E100.sketch_text.stroke-107"),sQuery(id+"F0.wireOp",EDGE,"E100.sketch_text.stroke-108"),sQuery(id+"F0.wireOp",EDGE,"E100.sketch_text.stroke-109"),sQuery(id+"F0.wireOp",EDGE,"E100.sketch_text.stroke-110"),sQuery(id+"F0.wireOp",EDGE,"E100.sketch_text.stroke-111"),sQuery(id+"F0.wireOp",EDGE,"E100.sketch_text.stroke-112"),sQuery(id+"F0.wireOp",EDGE,"E100.sketch_text.stroke-113"),sQuery(id+"F0.wireOp",EDGE,"E100.sketch_text.stroke-114"),sQuery(id+"F0.wireOp",EDGE,"E100.sketch_text.stroke-115"),sQuery(id+"F0.wireOp",EDGE,"E100.sketch_text.stroke-116"),sQuery(id+"F0.wireOp",EDGE,"E100.sketch_text.stroke-117"),sQuery(id+"F0.wireOp",EDGE,"E103"),sQuery(id+"F0.wireOp",EDGE,"E105"),sQuery(id+"F0.wireOp",EDGE,"E106"),sQuery(id+"F0.wireOp",EDGE,"E107")])],"isStart":true});
            var sketch = newSketch(context, id + "F2", { "sketchPlane" : qUnion([Q0])});
            skLineSegment(sketch, "E109.bottom", {"start": v(-16.59, 102.47) * mm, "end": v(157.53, 102.47) * mm});
            skLineSegment(sketch, "E109.top", {"start": v(-16.59, -15.66) * mm, "end": v(157.53, -15.66) * mm});
            skLineSegment(sketch, "E109.left", {"start": v(-16.59, 102.47) * mm, "end": v(-16.59, -15.66) * mm});
            skLineSegment(sketch, "E109.right", {"start": v(157.53, 102.47) * mm, "end": v(157.53, -15.66) * mm});
            skSolve(sketch);
        }
        {
            var Q0;
            Q0 = qSketchRegion(id + "F2", true);
            extrude(context, id + "F3", {"entities" : qUnion([Q0]), "operationType" : NewBodyOperationType.ADD, "oppositeDirection" : true, "depth" : 31.75 * mm});
        }
        {
            var Q0;
            Q0=makeQuery(id+"F3.boolean.opBoolean","SPLIT",FACE,{"disambiguationData":[TD([makeQuery(id+"F1.opExtrude","SWEPT_FACE",FACE,{"disambiguationData":[OSD([sQuery(id+"F0.wireOp",EDGE,"E8")])]})])],"derivedFrom":makeQuery(id+"F3.opExtrude","CAP_FACE",FACE,{"disambiguationData":[OSD([sQuery(id+"F2.wireOp",EDGE,"E109.bottom"),sQuery(id+"F2.wireOp",EDGE,"E109.top"),sQuery(id+"F2.wireOp",EDGE,"E109.left"),sQuery(id+"F2.wireOp",EDGE,"E109.right")])],"isStart":false})});
            var sketch = newSketch(context, id + "F4", { "sketchPlane" : qUnion([Q0])});
            skLineSegment(sketch, "E110.bottom", {"start": v(-101.34, 17.06) * mm, "end": v(-78.29, 17.06) * mm});
            skLineSegment(sketch, "E110.top", {"start": v(-101.34, 13.92) * mm, "end": v(-78.29, 13.92) * mm});
            skLineSegment(sketch, "E110.left", {"start": v(-101.34, 17.06) * mm, "end": v(-101.34, 13.92) * mm});
            skLineSegment(sketch, "E110.right", {"start": v(-78.29, 17.06) * mm, "end": v(-78.29, 13.92) * mm});
            skLineSegment(sketch, "E111", {"start": v(-101.34, 19.16) * mm, "end": v(-97.8, 19.16) * mm});
            skLineSegment(sketch, "E112", {"start": v(-97.8, 19.16) * mm, "end": v(-90.08, 32.26) * mm});
            skLineSegment(sketch, "E113", {"start": v(-90.08, 32.26) * mm, "end": v(-88.64, 30.04) * mm});
            skLineSegment(sketch, "E114", {"start": v(-88.64, 30.04) * mm, "end": v(-94.8, 19.16) * mm});
            skLineSegment(sketch, "E115", {"start": v(-94.8, 19.16) * mm, "end": v(-91.52, 19.16) * mm});
            skLineSegment(sketch, "E116", {"start": v(-91.52, 19.16) * mm, "end": v(-86.67, 27.28) * mm});
            skLineSegment(sketch, "E117", {"start": v(-86.67, 27.28) * mm, "end": v(-82.6, 19.16) * mm});
            skLineSegment(sketch, "E118", {"start": v(-82.6, 19.16) * mm, "end": v(-78.42, 19.16) * mm});
            skLineSegment(sketch, "E119", {"start": v(-78.42, 19.16) * mm, "end": v(-90.08, 38.42) * mm});
            skLineSegment(sketch, "E120", {"start": v(-90.08, 38.42) * mm, "end": v(-101.34, 19.16) * mm});
            skSolve(sketch);
        }
        {
            var Q0;
            Q0 = qSketchRegion(id + "F4", true);
            extrude(context, id + "F5", {"entities" : qUnion([Q0]), "operationType" : NewBodyOperationType.ADD, "depth" : 6.35 * mm});
        }
        {
            var Q0;
            Q0=makeQuery(id+"F1.opExtrude","CAP_EDGE",EDGE,{"disambiguationData":[OSD([sQuery(id+"F0.wireOp",EDGE,"E5")])],"isStart":false});
            var Q1;
            Q1=makeQuery(id+"F1.opExtrude","CAP_EDGE",EDGE,{"disambiguationData":[OSD([sQuery(id+"F0.wireOp",EDGE,"E7")])],"isStart":false});
            var Q2;
            Q2=makeQuery(id+"F1.opExtrude","CAP_EDGE",EDGE,{"disambiguationData":[OSD([sQuery(id+"F0.wireOp",EDGE,"E6")])],"isStart":false});
            var Q3;
            Q3=makeQuery(id+"F1.opExtrude","SWEPT_EDGE",EDGE,{"disambiguationData":[OSD([sQuery(id+"F0.wireOp",EDGE,"E5"),sQuery(id+"F0.wireOp",EDGE,"E7")])]});
            var Q4;
            Q4=makeQuery(id+"F1.opExtrude","SWEPT_EDGE",EDGE,{"disambiguationData":[OSD([sQuery(id+"F0.wireOp",EDGE,"E5"),sQuery(id+"F0.wireOp",EDGE,"E6")])]});
            var Q5;
            Q5=makeQuery(id+"F1.opExtrude","CAP_EDGE",EDGE,{"disambiguationData":[OSD([sQuery(id+"F0.wireOp",EDGE,"E5")])],"isStart":true});
            var Q6;
            Q6=makeQuery(id+"F1.opExtrude","CAP_EDGE",EDGE,{"disambiguationData":[OSD([sQuery(id+"F0.wireOp",EDGE,"E7")])],"isStart":true});
            var Q7;
            Q7=makeQuery(id+"F1.opExtrude","CAP_EDGE",EDGE,{"disambiguationData":[OSD([sQuery(id+"F0.wireOp",EDGE,"E6")])],"isStart":true});
            fillet(context, id + "F6", {"entities" : qUnion([Q0, Q1, Q2, Q3, Q4, Q5, Q6, Q7]), "radius" : 5.08 * mm, "tangentPropagation" : true, "allowEdgeOverflow" : false});
        }
        {
            var Q0;
            Q0=makeQuery(id+"F1.opExtrude","CAP_EDGE",EDGE,{"disambiguationData":[OSD([sQuery(id+"F0.wireOp",EDGE,"E3")])],"isStart":false});
            var Q1;
            Q1=makeQuery(id+"F1.opExtrude","CAP_EDGE",EDGE,{"disambiguationData":[OSD([sQuery(id+"F0.wireOp",EDGE,"E4")])],"isStart":false});
            var Q2;
            Q2=makeQuery(id+"F1.opExtrude","CAP_EDGE",EDGE,{"disambiguationData":[OSD([sQuery(id+"F0.wireOp",EDGE,"E4")])],"isStart":true});
            var Q3;
            Q3=makeQuery(id+"F1.opExtrude","SWEPT_EDGE",EDGE,{"disambiguationData":[OSD([sQuery(id+"F0.wireOp",EDGE,"E2"),sQuery(id+"F0.wireOp",EDGE,"E4")])]});
            var Q4;
            Q4=makeQuery(id+"F1.opExtrude","CAP_EDGE",EDGE,{"disambiguationData":[OSD([sQuery(id+"F0.wireOp",EDGE,"E3")])],"isStart":true});
            var Q5;
            Q5=makeQuery(id+"F1.opExtrude","SWEPT_FACE",FACE,{"disambiguationData":[OSD([sQuery(id+"F0.wireOp",EDGE,"E2")])]});
            fillet(context, id + "F7", {"entities" : qUnion([Q0, Q1, Q2, Q3, Q4, Q5]), "radius" : 5.08 * mm, "tangentPropagation" : true, "allowEdgeOverflow" : false});
        }
    });
